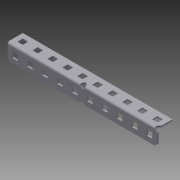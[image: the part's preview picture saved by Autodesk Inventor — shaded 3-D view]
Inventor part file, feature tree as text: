
AUTODESK INVENTOR PART (.ipt)
format: ipt  version: 2014 SP1 (Build 180222100, 222)  size: 1,351,168 bytes
history: native  units: in
note: dims shown in document units (in); Inventor stores cm internally (conversion verified against a paired STEP export)
features: extrude x2, sketch x2, other x1, imported_body x1
ambient origin geometry x8: Origin, YZ Plane, XZ Plane, XY Plane, X Axis, Y Axis, Z Axis, Center Point
bodies: Body1 (feature_tree)
feature tree (6):
  parser-record x1  (decoder bookkeeping rows leaked as tree rows — omitted from the tree; the rows remain in map.json)
  imported_body  "Base1"
  extrude  "Extrusion1"  Depth=0.432in
  extrude  "Extrusion2"  [1 undecoded]
  sketch  "Sketch1"  dims[d0=1.0in d1=0.0in d2=0.432in]
  sketch  "Sketch2"  dims[d3=1.0in d4=0.0in]
note: 1 required parameter value undecoded (feature->parameter linkage not recoverable at this tier; creation-order binding heuristic only, values carry confidence <= 0.55)
